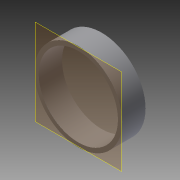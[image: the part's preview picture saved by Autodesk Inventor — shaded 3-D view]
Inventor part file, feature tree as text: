
AUTODESK INVENTOR PART (.ipt)
format: ipt  version: 2014 (Build 180170000, 170)  size: 176,640 bytes
history: native  units: in
note: dims shown in document units (in); Inventor stores cm internally (conversion verified against a paired STEP export)
features: sketch x5, extrude x5, fillet x3, plane x2, reference x1, projected_geometry x1
ambient origin geometry x8: Origin, YZ Plane, XZ Plane, XY Plane, X Axis, Y Axis, Z Axis, Center Point
bodies: Solid1 (feature_tree)
feature tree (17):
  plane  "Work Plane1"
  sketch  "Sketch1"  dims[d0=0.01in d1=0.1in]
  plane  "Work Plane2"
  extrude  "Extrusion1"  Depth=0.1in
  sketch  "Sketch2"  dims[d2=1.0in d3=0.0in d4=0.1in d7=0.65in d8=0.65in d9=0.65in]
  extrude  "Extrusion3"  Depth=0.1in
  fillet  "Fillet1"  Radius=0.65in
  fillet  "Fillet2"  Radius=0.65in
  fillet  "Fillet3"  Radius=0.65in
  extrude  "Extrusion4"  Depth=0.15in TaperAngle=0.0deg
  extrude  "Extrusion5"  Depth=0.125in
  extrude  "Extrusion6"  Depth=0.1in
  reference  "Reference1"
  sketch  "Sketch3"  dims[d10=0.325in d11=0.15in d12=0.0in]
  sketch  "Sketch4"  dims[d13=0.25in d14=0.125in]
  projected_geometry  "Projected Loop1"
  sketch  "Sketch5"  dims[d15=0.125in d16=0.315in d17=0.25in d18=0.25in d19=0.15in d20=0.0in d21=0.2in d22=0.0in d23=0.1in d24=0.1in d25=0.0in]
